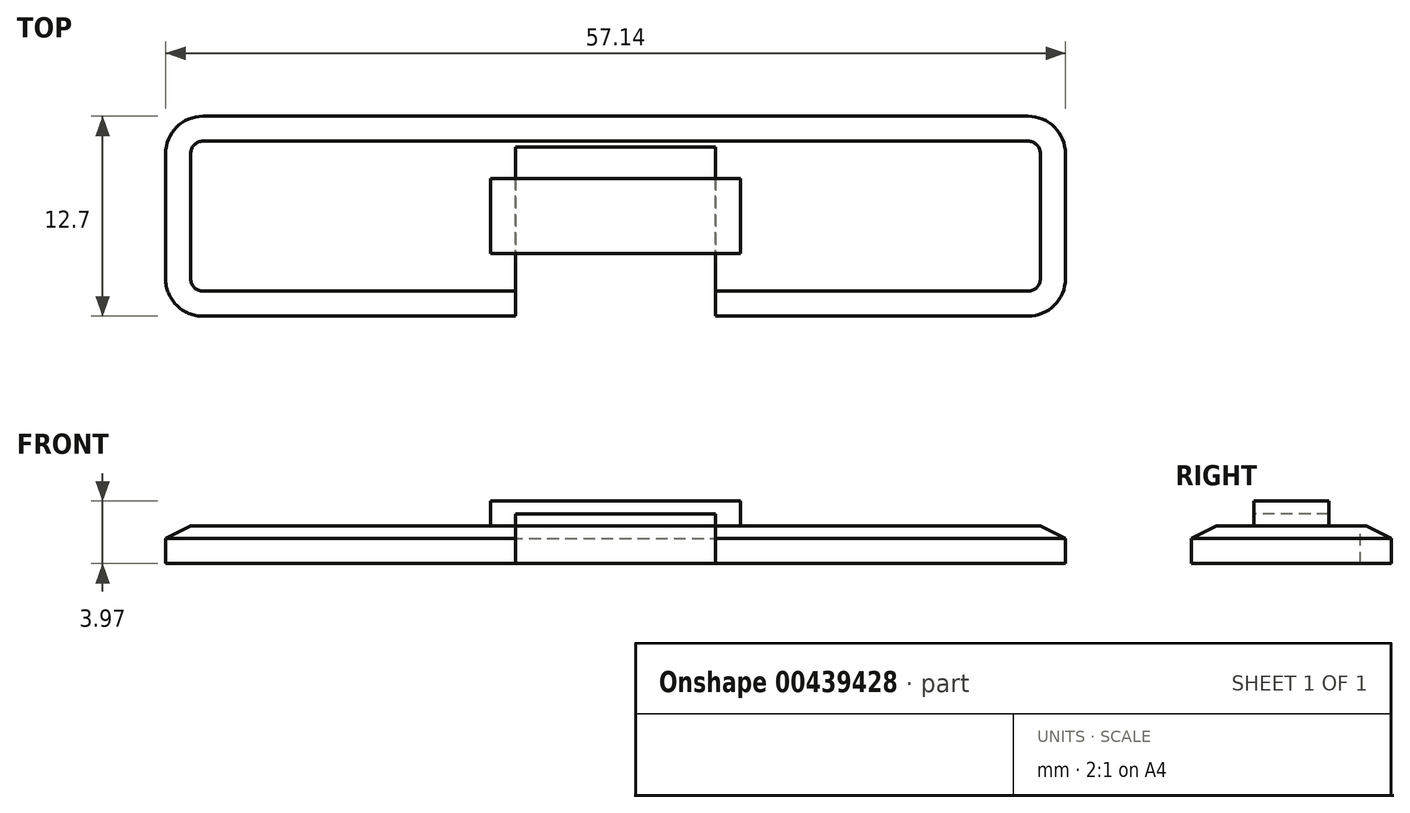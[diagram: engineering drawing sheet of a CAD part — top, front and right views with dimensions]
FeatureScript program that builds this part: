
annotation { "Feature Type Name" : "Feature", "Feature Type Description" : "" }
export const myFeature = defineFeature(function(context is Context, id is Id, definition is map)
    precondition{}
    {
        {
            var Q0;
            Q0=qCreatedBy(makeId("Top.planeOp"),FACE);
            var sketch = newSketch(context, id + "F0", { "sketchPlane" : qUnion([Q0])});
            skLineSegment(sketch, "E0.bottom", {"start": v(28.58, 6.35) * mm, "end": v(-28.58, 6.35) * mm});
            skLineSegment(sketch, "E0.top", {"start": v(28.58, -6.35) * mm, "end": v(-28.58, -6.35) * mm});
            skLineSegment(sketch, "E0.left", {"start": v(28.58, 6.35) * mm, "end": v(28.58, -6.35) * mm});
            skLineSegment(sketch, "E0.right", {"start": v(-28.58, 6.35) * mm, "end": v(-28.58, -6.35) * mm});
            skPoint(sketch, "E0.middle", {"position": v(0, 0) * mm});
            skLineSegment(sketch, "E1", {"start": v(0, -6.35) * mm, "end": v(0, 12.7) * mm, "construction": true});
            skSolve(sketch);
        }
        {
            var Q0;
            Q0=qSketchRegion(id+"F0",true);
            extrude(context, id + "F1", {"entities" : qUnion([Q0]), "depth" : 2.38 * mm});
        }
        {
            var Q0;
            Q0=makeQuery(id+"F1.opExtrude","CAP_FACE",FACE,{"disambiguationData":[OSD([sQuery(id+"F0.wireOp",EDGE,"E0.bottom"),sQuery(id+"F0.wireOp",EDGE,"E0.top"),sQuery(id+"F0.wireOp",EDGE,"E0.left"),sQuery(id+"F0.wireOp",EDGE,"E0.right"),sQuery(id+"F0.wireOp",EDGE,"sQ5FOiL1-PATm-f4FL-sMBU-Sejo3Ob4zhOJ.top"),sQuery(id+"F0.wireOp",EDGE,"eE3g78Th-Uhqz-HL4B-METg-kGSabsW8tSUq"),sQuery(id+"F0.wireOp",EDGE,"LGPMkXvS-dz4y-Jq5w-iaXi-xn5e82dF6vV4"),sQuery(id+"F0.wireOp",EDGE,"e5298548-960a-4d00-80d0-4a68bccc32c3.trimOffspring")])],"isStart":false});
            var sketch = newSketch(context, id + "F2", { "sketchPlane" : qUnion([Q0])});
            skLineSegment(sketch, "E2.bottom", {"start": v(-7.94, 2.38) * mm, "end": v(7.94, 2.38) * mm});
            skLineSegment(sketch, "E2.top", {"start": v(-7.94, -2.38) * mm, "end": v(7.94, -2.38) * mm});
            skLineSegment(sketch, "E2.left", {"start": v(-7.94, 2.38) * mm, "end": v(-7.94, -2.38) * mm});
            skLineSegment(sketch, "E2.right", {"start": v(7.94, 2.38) * mm, "end": v(7.94, -2.38) * mm});
            skPoint(sketch, "E2.middle", {"position": v(0, 0) * mm});
            skSolve(sketch);
        }
        {
            var Q0;
            Q0=qSketchRegion(id+"F2",true);
            extrude(context, id + "F3", {"entities" : qUnion([Q0]), "operationType" : NewBodyOperationType.ADD, "depth" : 1.59 * mm});
        }
        {
            var Q0;
            Q0=makeQuery(id+"F3.opExtrude","CAP_FACE",FACE,{"disambiguationData":[OSD([sQuery(id+"F2.wireOp",EDGE,"E2.bottom"),sQuery(id+"F2.wireOp",EDGE,"E2.top"),sQuery(id+"F2.wireOp",EDGE,"E2.left"),sQuery(id+"F2.wireOp",EDGE,"E2.right")])],"isStart":false});
            cPlane(context, id + "F4", {"entities" : qUnion([Q0]), "cplaneType" : CPlaneType.OFFSET, "offset" : 0.8 * mm, "oppositeDirection" : true, "width" : 152.4 * mm, "height" : 152.4 * mm});
        }
        {
            var Q0;
            Q0=qCreatedBy(id+"F4.planeOp",FACE);
            var sketch = newSketch(context, id + "F5", { "sketchPlane" : qUnion([Q0])});
            skLineSegment(sketch, "E3.0.1", {"start": v(-6.35, -2.38) * mm, "end": v(6.35, -2.38) * mm});
            skLineSegment(sketch, "E3.0.3", {"start": v(6.35, 2.38) * mm, "end": v(-6.35, 2.38) * mm});
            skLineSegment(sketch, "E4", {"start": v(-6.35, 2.38) * mm, "end": v(-6.35, -2.38) * mm});
            skLineSegment(sketch, "E5", {"start": v(6.35, 2.38) * mm, "end": v(6.35, -2.38) * mm});
            skLineSegment(sketch, "E6", {"start": v(0, 2.38) * mm, "end": v(0, -2.38) * mm, "construction": true});
            skSolve(sketch);
        }
        {
            var Q0;
            Q0=qSketchRegion(id+"F5",true);
            var Q1;
            Q1=makeQuery(id+"F1.opExtrude","CAP_FACE",FACE,{"disambiguationData":[OSD([sQuery(id+"F0.wireOp",EDGE,"E0.bottom"),sQuery(id+"F0.wireOp",EDGE,"E0.top"),sQuery(id+"F0.wireOp",EDGE,"E0.left"),sQuery(id+"F0.wireOp",EDGE,"E0.right"),sQuery(id+"F0.wireOp",EDGE,"sQ5FOiL1-PATm-f4FL-sMBU-Sejo3Ob4zhOJ.top"),sQuery(id+"F0.wireOp",EDGE,"eE3g78Th-Uhqz-HL4B-METg-kGSabsW8tSUq"),sQuery(id+"F0.wireOp",EDGE,"LGPMkXvS-dz4y-Jq5w-iaXi-xn5e82dF6vV4"),sQuery(id+"F0.wireOp",EDGE,"e5298548-960a-4d00-80d0-4a68bccc32c3.trimOffspring")])],"isStart":true});
            extrude(context, id + "F6", {"entities" : qUnion([Q0]), "operationType" : NewBodyOperationType.REMOVE, "endBound" : BoundingType.UP_TO_SURFACE, "oppositeDirection" : true, "endBoundEntityFace" : qUnion([Q1]), "depth" : 0.8 * mm});
        }
        {
            var Q0;
            Q0=makeQuery(id+"F1.opExtrude","CAP_FACE",FACE,{"disambiguationData":[OSD([sQuery(id+"F0.wireOp",EDGE,"E0.bottom"),sQuery(id+"F0.wireOp",EDGE,"E0.top"),sQuery(id+"F0.wireOp",EDGE,"E0.left"),sQuery(id+"F0.wireOp",EDGE,"E0.right"),sQuery(id+"F0.wireOp",EDGE,"sQ5FOiL1-PATm-f4FL-sMBU-Sejo3Ob4zhOJ.top"),sQuery(id+"F0.wireOp",EDGE,"eE3g78Th-Uhqz-HL4B-METg-kGSabsW8tSUq"),sQuery(id+"F0.wireOp",EDGE,"LGPMkXvS-dz4y-Jq5w-iaXi-xn5e82dF6vV4"),sQuery(id+"F0.wireOp",EDGE,"e5298548-960a-4d00-80d0-4a68bccc32c3.trimOffspring")])],"isStart":false});
            var sketch = newSketch(context, id + "F7", { "sketchPlane" : qUnion([Q0])});
            skLineSegment(sketch, "E7.bottom", {"start": v(-6.35, -2.38) * mm, "end": v(6.35, -2.38) * mm});
            skLineSegment(sketch, "E7.top", {"start": v(-6.35, -6.35) * mm, "end": v(6.35, -6.35) * mm});
            skLineSegment(sketch, "E7.left", {"start": v(-6.35, -2.38) * mm, "end": v(-6.35, -6.35) * mm});
            skLineSegment(sketch, "E7.right", {"start": v(6.35, -2.38) * mm, "end": v(6.35, -6.35) * mm});
            skSolve(sketch);
        }
        {
            var Q0;
            Q0 = qSketchRegion(id + "F7", true);
            extrude(context, id + "F8", {"entities" : qUnion([Q0]), "operationType" : NewBodyOperationType.REMOVE, "endBound" : BoundingType.THROUGH_ALL, "oppositeDirection" : true, "depth" : 25 * mm});
        }
        {
            var Q0;
            Q0=makeQuery(id+"F1.opExtrude","CAP_FACE",FACE,{"disambiguationData":[OSD([sQuery(id+"F0.wireOp",EDGE,"E0.bottom"),sQuery(id+"F0.wireOp",EDGE,"E0.top"),sQuery(id+"F0.wireOp",EDGE,"E0.left"),sQuery(id+"F0.wireOp",EDGE,"E0.right"),sQuery(id+"F0.wireOp",EDGE,"sQ5FOiL1-PATm-f4FL-sMBU-Sejo3Ob4zhOJ.top"),sQuery(id+"F0.wireOp",EDGE,"eE3g78Th-Uhqz-HL4B-METg-kGSabsW8tSUq"),sQuery(id+"F0.wireOp",EDGE,"LGPMkXvS-dz4y-Jq5w-iaXi-xn5e82dF6vV4"),sQuery(id+"F0.wireOp",EDGE,"e5298548-960a-4d00-80d0-4a68bccc32c3.trimOffspring")])],"isStart":false});
            var sketch = newSketch(context, id + "F9", { "sketchPlane" : qUnion([Q0])});
            skLineSegment(sketch, "E8.bottom", {"start": v(-6.35, 2.38) * mm, "end": v(6.35, 2.38) * mm});
            skLineSegment(sketch, "E8.top", {"start": v(-6.35, 4.38) * mm, "end": v(6.35, 4.38) * mm});
            skLineSegment(sketch, "E8.left", {"start": v(-6.35, 2.38) * mm, "end": v(-6.35, 4.38) * mm});
            skLineSegment(sketch, "E8.right", {"start": v(6.35, 2.38) * mm, "end": v(6.35, 4.38) * mm});
            skSolve(sketch);
        }
        {
            var Q0;
            Q0 = qSketchRegion(id + "F9", true);
            extrude(context, id + "F10", {"entities" : qUnion([Q0]), "operationType" : NewBodyOperationType.REMOVE, "endBound" : BoundingType.THROUGH_ALL, "oppositeDirection" : true, "depth" : 25 * mm});
        }
        {
            var Q0;
            Q0=makeQuery(id+"F6.boolean.opBoolean","COPY",FACE,{"derivedFrom":makeQuery(id+"F6.opExtrude","CAP_FACE",FACE,{"disambiguationData":[OSD([sQuery(id+"F5.wireOp",EDGE,"E3.0.1"),sQuery(id+"F5.wireOp",EDGE,"E3.0.3"),sQuery(id+"F5.wireOp",EDGE,"E4"),sQuery(id+"F5.wireOp",EDGE,"E5")])],"isStart":true})});
            var sketch = newSketch(context, id + "F11", { "sketchPlane" : qUnion([Q0])});
            skLineSegment(sketch, "E9.0.0", {"start": v(6.35, -2.38) * mm, "end": v(6.35, 2.38) * mm});
            skLineSegment(sketch, "E9.0.1", {"start": v(6.35, 2.38) * mm, "end": v(-6.35, 2.38) * mm});
            skLineSegment(sketch, "E9.0.2", {"start": v(-6.35, 2.38) * mm, "end": v(-6.35, -2.38) * mm});
            skLineSegment(sketch, "E9.0.3", {"start": v(-6.35, -2.38) * mm, "end": v(6.35, -2.38) * mm});
            skSolve(sketch);
        }
        {
            var Q0;
            Q0 = qSketchRegion(id + "F11", true);
            extrude(context, id + "F12", {"entities" : qUnion([Q0]), "operationType" : NewBodyOperationType.ADD, "depth" : 1 / 406.4 * mm});
        }
        {
            var Q0;
            Q0=makeQuery(id+"F1.opExtrude","SWEPT_EDGE",EDGE,{"disambiguationData":[OSD([sQuery(id+"F0.wireOp",EDGE,"E0.top"),sQuery(id+"F0.wireOp",EDGE,"E0.right")])]});
            var Q1;
            Q1=makeQuery(id+"F1.opExtrude","SWEPT_EDGE",EDGE,{"disambiguationData":[OSD([sQuery(id+"F0.wireOp",EDGE,"E0.top"),sQuery(id+"F0.wireOp",EDGE,"E0.left")])]});
            var Q2;
            Q2=makeQuery(id+"F1.opExtrude","SWEPT_EDGE",EDGE,{"disambiguationData":[OSD([sQuery(id+"F0.wireOp",EDGE,"E0.bottom"),sQuery(id+"F0.wireOp",EDGE,"E0.left")])]});
            var Q3;
            Q3=makeQuery(id+"F1.opExtrude","SWEPT_EDGE",EDGE,{"disambiguationData":[OSD([sQuery(id+"F0.wireOp",EDGE,"sQ5FOiL1-PATm-f4FL-sMBU-Sejo3Ob4zhOJ.top"),sQuery(id+"F0.wireOp",EDGE,"LGPMkXvS-dz4y-Jq5w-iaXi-xn5e82dF6vV4")])]});
            var Q4;
            Q4=makeQuery(id+"F1.opExtrude","SWEPT_EDGE",EDGE,{"disambiguationData":[OSD([sQuery(id+"F0.wireOp",EDGE,"E0.right"),sQuery(id+"F0.wireOp",EDGE,"e5298548-960a-4d00-80d0-4a68bccc32c3.trimOffspring")])]});
            var Q5;
            Q5=makeQuery(id+"F1.opExtrude","SWEPT_EDGE",EDGE,{"disambiguationData":[OSD([sQuery(id+"F0.wireOp",EDGE,"sQ5FOiL1-PATm-f4FL-sMBU-Sejo3Ob4zhOJ.top"),sQuery(id+"F0.wireOp",EDGE,"eE3g78Th-Uhqz-HL4B-METg-kGSabsW8tSUq")])]});
            var Q6;
            Q6=makeQuery(id+"F1.opExtrude","SWEPT_EDGE",EDGE,{"disambiguationData":[OSD([sQuery(id+"F0.wireOp",EDGE,"eE3g78Th-Uhqz-HL4B-METg-kGSabsW8tSUq"),sQuery(id+"F0.wireOp",EDGE,"e5298548-960a-4d00-80d0-4a68bccc32c3.trimOffspring")])]});
            var Q7;
            Q7=makeQuery(id+"F1.opExtrude","SWEPT_EDGE",EDGE,{"disambiguationData":[OSD([sQuery(id+"F0.wireOp",EDGE,"E0.bottom"),sQuery(id+"F0.wireOp",EDGE,"LGPMkXvS-dz4y-Jq5w-iaXi-xn5e82dF6vV4")])]});
            fillet(context, id + "F13", {"entities" : qUnion([Q0, Q1, Q2, Q3, Q4, Q5, Q6, Q7]), "radius" : 2.38 * mm, "tangentPropagation" : true, "allowEdgeOverflow" : false});
        }
        {
            var Q0;
            Q0=makeQuery(id+"F1.opExtrude","CAP_EDGE",EDGE,{"disambiguationData":[OSD([sQuery(id+"F0.wireOp",EDGE,"E0.bottom")])],"isStart":false});
            chamfer(context, id + "F14", {"entities" : qUnion([Q0]), "chamferType" : ChamferType.TWO_OFFSETS, "width1" : 1.59 * mm, "oppositeDirection" : false, "width2" : 0.8 * mm, "tangentPropagation" : true});
        }
    });
